# Revit family: TRP
name_source: partatom
category: Lighting Fixtures
revit_build: Autodesk Revit 2013 (Build: 20120221_2030(x64)
units: mm (PartAtom-declared; Revit-internal decimal feet)

## types (7) — shared parameters
Apparent Load = 34 VA
Color Filter = 16777215
Default Elevation = 48 "
Description = Architectural Geometric Wallpack Sconce
Dimming Lamp Color Temperature Shift = <None>
Emit Shape Visible in Rendering = No
Emit from Rectangle Length = 5 "
Emit from Rectangle Width = 7 "
Lamp = LED
Load Classification = Lighting
Manufacturer = Hubbell Outdoor Lighting
Manufacturer Fax = 864-678-1065
Model = TRP Geo Sconce LED Large
Opal lens = Hubbell-Glass
Photometric Web File = TRP-30L3K-035-2.IES
Power Factor = 1
Product Documentation Link = http://cdn.hubbelloutdoor.com
Product Page URL = http://www.hubbelloutdoor.com
Tilt Angle = 90.00°
URL = http://www.hubbelloutdoor.com
Voltage = 120 V
Wattage Comments = 34W/53W/68W
Watts = 34 W

## per-type parameters (varying)
| type | Finish |
| TRP-BL | Hubbell-Black |
| TRP-DB | Hubbell-Bronze |
| TRP-FG | Hubbell-Forest Green |
| TRP-GR | Hubbell-Gray |
| TRP-PS | Hubbell-Platinum |
| TRP-RD | Hubbell-Red |
| TRP-WH | Hubbell-White |

## geometry (parser evidence)
native form markers: Blend x10, Sweep x1
no freeform markers — native parametric forms only
